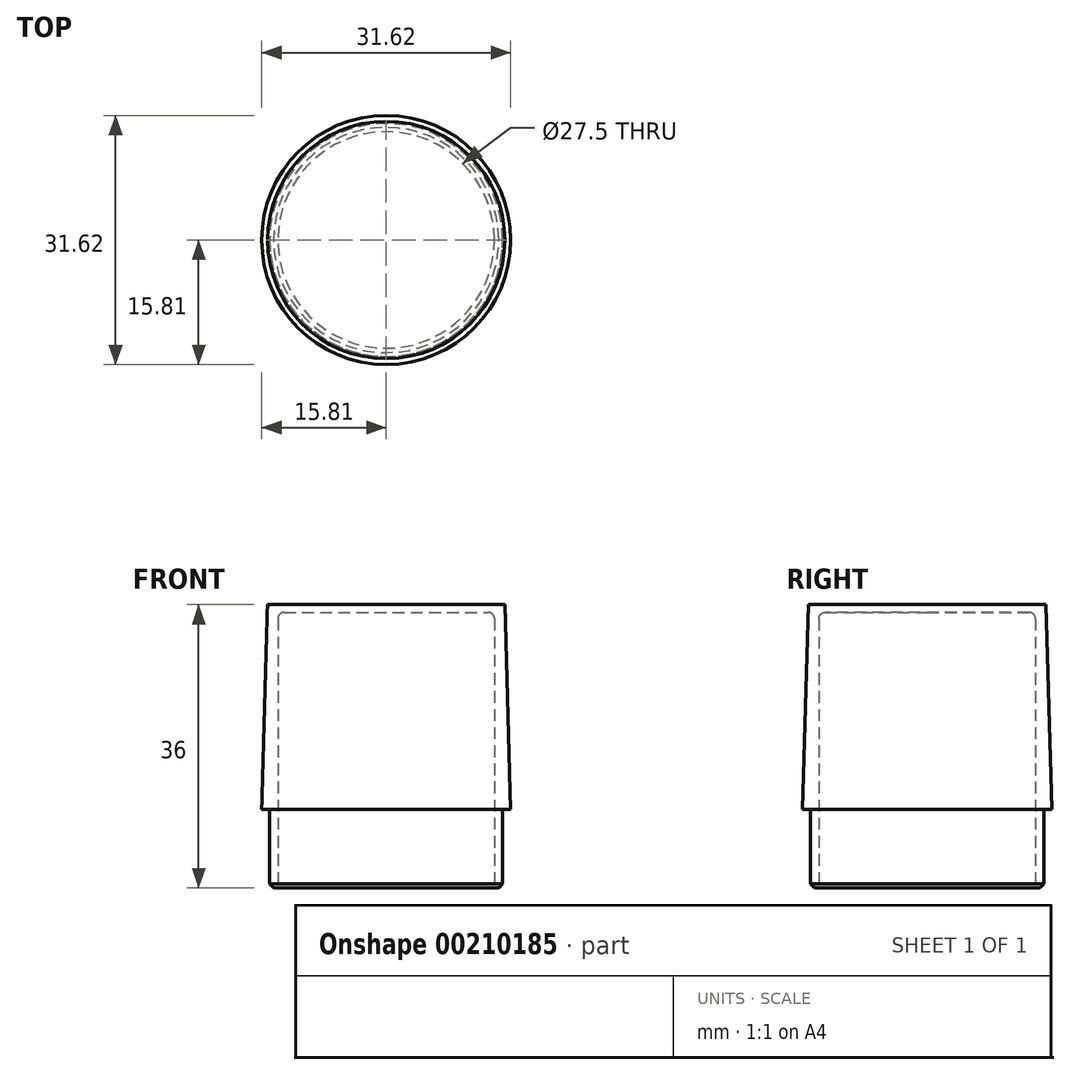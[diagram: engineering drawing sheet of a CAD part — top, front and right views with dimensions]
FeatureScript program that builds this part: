
annotation { "Feature Type Name" : "Feature", "Feature Type Description" : "" }
export const myFeature = defineFeature(function(context is Context, id is Id, definition is map)
    precondition{}
    {
        {
            var Q0;
            Q0=qCreatedBy(makeId("Front.planeOp"),FACE);
            var sketch = newSketch(context, id + "F0", { "sketchPlane" : qUnion([Q0]), "disableImprinting" : false});
            skLineSegment(sketch, "E0", {"start": v(0, 0) * mm, "end": v(0, 70.58) * mm});
            skLineSegment(sketch, "E1", {"start": v(0, 0) * mm, "end": v(-13, 0) * mm});
            skLineSegment(sketch, "E2.MirrorCS", {"start": v(0, 1) * mm, "end": v(0, 0) * mm});
            skLineSegment(sketch, "E3.MirrorCS", {"start": v(0, 0) * mm, "end": v(-12.96, 0) * mm});
            skLineSegment(sketch, "E4.MirrorCS", {"start": v(0, 1) * mm, "end": v(-15.07, 1) * mm});
            skPoint(sketch, "E5.filletArc.end.orphan", {"position": v(-14, -1) * mm});
            skPoint(sketch, "E5.filletArc.start.orphan", {"position": v(-15, 0) * mm});
            skPoint(sketch, "E6.filletArc.start.orphan", {"position": v(-14, 1) * mm});
            skPoint(sketch, "E7.start.orphan", {"position": v(0, -1) * mm});
            skPoint(sketch, "E8.MirrorCS.end.orphan", {"position": v(-15.71, -25) * mm});
            skPoint(sketch, "E9.orphan", {"position": v(-15.74, -25) * mm});
            skPoint(sketch, "E10.MirrorCS.start.orphan", {"position": v(-15, -25) * mm});
            skPoint(sketch, "E11.orphan", {"position": v(-15, -35) * mm});
            skLineSegment(sketch, "E12.0", {"start": v(-15.07, 1) * mm, "end": v(-15.81, -25) * mm});
            skLineSegment(sketch, "E13.0", {"start": v(-13.75, -0.8) * mm, "end": v(-13.75, -35) * mm});
            skLineSegment(sketch, "E14.0", {"start": v(-14.8, -25) * mm, "end": v(-14.8, -35) * mm});
            skLineSegment(sketch, "E15", {"start": v(-15.81, -25) * mm, "end": v(-14.8, -25) * mm});
            skPoint(sketch, "E16.orphan", {"position": v(-16.02, -25) * mm});
            skPoint(sketch, "E17.MirrorCS.start.orphan", {"position": v(-14, -35) * mm});
            skLineSegment(sketch, "E18", {"start": v(-14.8, -35) * mm, "end": v(-13.75, -35) * mm});
            skPoint(sketch, "E19.orphan", {"position": v(-13, 0) * mm});
            skPoint(sketch, "E20.visualSharp", {"position": v(-13.75, 0) * mm});
            skArc(sketch, "E20.filletArc", {"start": v(-12.96, 0) * mm, "mid": v(-13.52, -0.23) * mm, "end": v(-13.75, -0.8) * mm});
            skSolve(sketch);
        }
        {
            var Q0;
            Q0 = qSketchRegion(id + "F0", true);
            var Q1;
            Q1=sQuery(id+"F0.wireOp",EDGE,"E0");
            revolve(context, id + "F1", {"entities" : qUnion([Q0]), "axis" : qUnion([Q1]), "revolveType" : RevolveType.FULL});
        }
        {
            var Q0;
            Q0=makeQuery(id+"F1.opRevolve","SWEPT_EDGE",EDGE,{"disambiguationData":[OSD([sQuery(id+"F0.wireOp",EDGE,"E14.0"),sQuery(id+"F0.wireOp",EDGE,"E18")])]});
            chamfer(context, id + "F2", {"entities" : qUnion([Q0]), "width" : 0.5 * mm, "tangentPropagation" : true});
        }
    });
